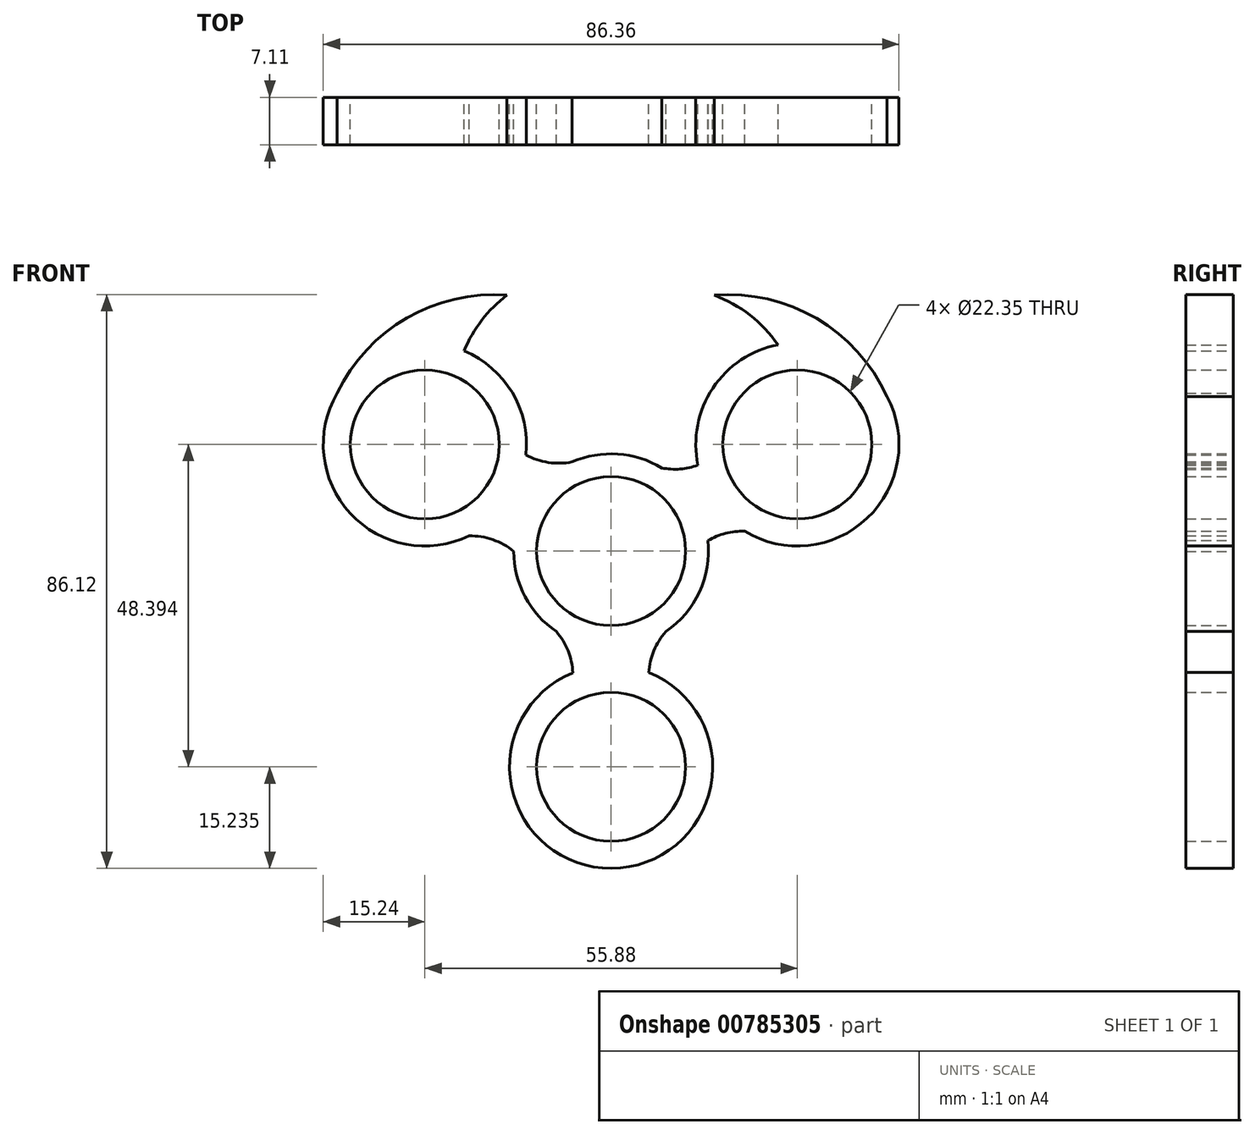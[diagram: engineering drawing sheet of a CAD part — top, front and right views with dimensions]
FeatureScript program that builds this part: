
annotation { "Feature Type Name" : "Feature", "Feature Type Description" : "" }
export const myFeature = defineFeature(function(context is Context, id is Id, definition is map)
    precondition{}
    {
        {
            var Q0;
            Q0=qCreatedBy(makeId("Front.planeOp"),FACE);
            var sketch = newSketch(context, id + "F0", { "sketchPlane" : qUnion([Q0])});
            skCircle(sketch, "E0", {"center": v(0, 0) * mm, "radius": 14.6 * mm});
            skCircle(sketch, "E1", {"center": v(0, -32.38) * mm, "radius": 15.24 * mm});
            skArc(sketch, "E2", {"start": v(8.2, -12.08) * mm, "mid": v(6.41, -14.94) * mm, "end": v(5.65, -18.23) * mm});
            skArc(sketch, "E3.MirrorCS", {"start": v(-8.2, -12.08) * mm, "mid": v(-6.46, -14.97) * mm, "end": v(-5.74, -18.27) * mm});
            skCircle(sketch, "E4", {"center": v(-27.94, 16) * mm, "radius": 15.24 * mm});
            skArc(sketch, "E5", {"start": v(-14.6, -0.05) * mm, "mid": v(-17.75, 1.72) * mm, "end": v(-21.32, 2.28) * mm});
            skArc(sketch, "E6.MirrorCS", {"start": v(-3.42, 14.2) * mm, "mid": v(-8.13, 13.2) * mm, "end": v(-12.78, 14.45) * mm});
            skArc(sketch, "E7.MirrorCS", {"start": v(3.68, 14.13) * mm, "mid": v(8.2, 12.38) * mm, "end": v(13.02, 12.9) * mm});
            skArc(sketch, "E8.MirrorCS", {"start": v(14.52, 1.57) * mm, "mid": v(17.18, 2.67) * mm, "end": v(20.04, 2.98) * mm});
            skCircle(sketch, "E9.MirrorC", {"center": v(27.94, 16) * mm, "radius": 15.24 * mm});
            skArc(sketch, "E10", {"start": v(-15.61, 38.4) * mm, "mid": v(-30.65, 35) * mm, "end": v(-41.11, 23.67) * mm});
            skArc(sketch, "E11", {"start": v(-15.61, 38.4) * mm, "mid": v(-19.4, 34.66) * mm, "end": v(-22.06, 30.07) * mm});
            skArc(sketch, "E12.MirrorCS", {"start": v(15.46, 38.4) * mm, "mid": v(30.83, 34.92) * mm, "end": v(41.37, 23.21) * mm});
            skArc(sketch, "E13.MirrorCS", {"start": v(15.46, 38.4) * mm, "mid": v(20.82, 35.42) * mm, "end": v(25.04, 30.97) * mm});
            skCircle(sketch, "E14", {"center": v(-27.94, 16) * mm, "radius": 11.18 * mm});
            skCircle(sketch, "E15", {"center": v(27.94, 16) * mm, "radius": 11.18 * mm});
            skCircle(sketch, "E16", {"center": v(0, 0) * mm, "radius": 11.18 * mm});
            skCircle(sketch, "E17", {"center": v(0, -32.38) * mm, "radius": 11.18 * mm});
            skSolve(sketch);
        }
        {
            var Q0;
            Q0=qSketchRegion(id+"F0",true);
            extrude(context, id + "F1", {"entities" : qUnion([Q0]), "depth" : 7.11 * mm, "offsetDistance" : 25.4 * mm});
        }
    });
